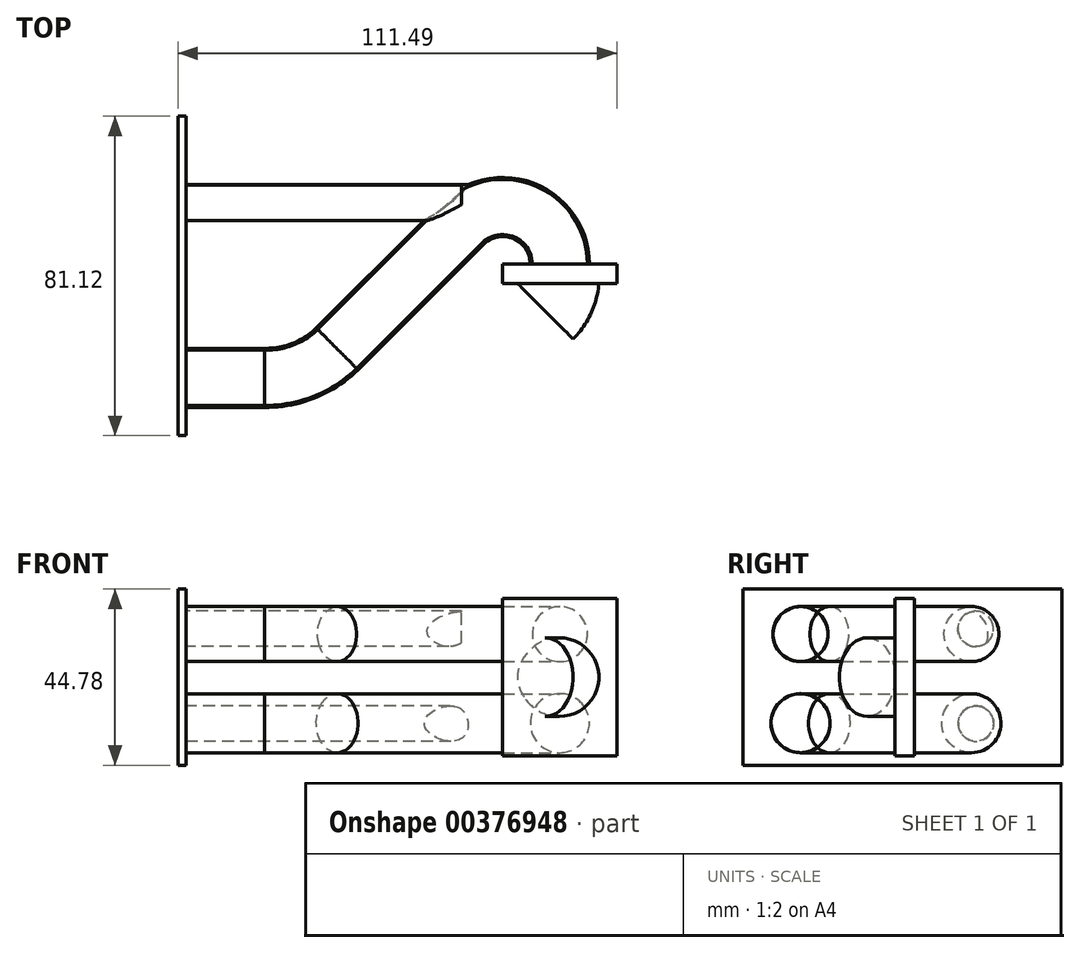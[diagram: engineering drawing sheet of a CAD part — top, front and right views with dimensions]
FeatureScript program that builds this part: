
annotation { "Feature Type Name" : "Feature", "Feature Type Description" : "" }
export const myFeature = defineFeature(function(context is Context, id is Id, definition is map)
    precondition{}
    {
        {
            var Q0;
            Q0=qCreatedBy(makeId("Front.planeOp"),FACE);
            var sketch = newSketch(context, id + "F0", { "sketchPlane" : qUnion([Q0])});
            skCircle(sketch, "E0", {"center": v(0, 0) * mm, "radius": 10 * mm});
            skLineSegment(sketch, "E1", {"start": v(-12.69, 8.58) * mm, "end": v(-12.69, -10.57) * mm});
            skSolve(sketch);
        }
        {
            var Q0;
            Q0=makeQuery(id+"F0.imprint","IMPRINT",FACE,{"disambiguationData":[TD([[makeQuery(id+"F0.imprint","IMPRINT",EDGE,{"derivedFrom":sQuery(id+"F0.wireOp",EDGE,"E0")}),1.0]])]});
            var Q1;
            Q1=sQuery(id+"F0.wireOp",EDGE,"E1");
            revolve(context, id + "F1", {"entities" : qUnion([Q0]), "axis" : qUnion([Q1]), "revolveType" : RevolveType.ONE_DIRECTION, "angle" : 45 * degree});
        }
        {
            var Q0;
            Q0=qCreatedBy(makeId("Front.planeOp"),FACE);
            var sketch = newSketch(context, id + "F2", { "sketchPlane" : qUnion([Q0])});
            skLineSegment(sketch, "E2.bottom", {"start": v(14.5, -20) * mm, "end": v(-14.5, -20) * mm});
            skLineSegment(sketch, "E2.top", {"start": v(14.5, 20) * mm, "end": v(-14.5, 20) * mm});
            skLineSegment(sketch, "E2.left", {"start": v(14.5, -20) * mm, "end": v(14.5, 20) * mm});
            skLineSegment(sketch, "E2.right", {"start": v(-14.5, -20) * mm, "end": v(-14.5, 20) * mm});
            skPoint(sketch, "E2.middle", {"position": v(0, 0) * mm});
            skSolve(sketch);
        }
        {
            var Q0;
            Q0=makeQuery(id+"F2.imprint","IMPRINT",FACE,{"disambiguationData":[TD([[makeQuery(id+"F2.imprint","IMPRINT",EDGE,{"derivedFrom":sQuery(id+"F2.wireOp",EDGE,"E2.bottom")}),-1.0]])]});
            extrude(context, id + "F3", {"entities" : qUnion([Q0]), "operationType" : NewBodyOperationType.ADD, "oppositeDirection" : true, "depth" : 3 * mm, "hasSecondDirection" : true, "secondDirectionOppositeDirection" : false, "secondDirectionDepth" : 1.9 * mm});
        }
        {
            var Q0;
            Q0=makeQuery(id+"F3.opExtrude","CAP_FACE",FACE,{"disambiguationData":[OSD([sQuery(id+"F2.wireOp",EDGE,"E2.bottom"),sQuery(id+"F2.wireOp",EDGE,"E2.top"),sQuery(id+"F2.wireOp",EDGE,"E2.left"),sQuery(id+"F2.wireOp",EDGE,"E2.right")])],"isStart":false});
            var sketch = newSketch(context, id + "F4", { "sketchPlane" : qUnion([Q0])});
            skPoint(sketch, "E3", {"position": v(0, -20) * mm});
            skLineSegment(sketch, "E4", {"start": v(0, -20) * mm, "end": v(0, 0) * mm});
            skPoint(sketch, "E5", {"position": v(0, -10) * mm});
            skPoint(sketch, "E6", {"position": v(0, 0) * mm});
            skSolve(sketch);
        }
        {
            var Q0;
            Q0=makeQuery(id+"F4.imprint","IMPRINT",FACE,{"disambiguationData":[TD([[makeQuery(id+"F4.imprint","IMPRINT",EDGE,{"derivedFrom":makeQuery(id+"F3.opExtrude","CAP_EDGE",EDGE,{"disambiguationData":[OSD([sQuery(id+"F2.wireOp",EDGE,"E2.top")])],"isStart":false})}),-1.0]])]});
            var sketch = newSketch(context, id + "F5", { "sketchPlane" : qUnion([Q0])});
            skCircle(sketch, "E7", {"center": v(0, -11.7) * mm, "radius": 7.5 * mm});
            skSolve(sketch);
        }
        {
            var Q0;
            Q0=makeQuery(id+"F4.imprint","IMPRINT",FACE,{"disambiguationData":[TD([[makeQuery(id+"F4.imprint","IMPRINT",EDGE,{"derivedFrom":makeQuery(id+"F3.opExtrude","CAP_EDGE",EDGE,{"disambiguationData":[OSD([sQuery(id+"F2.wireOp",EDGE,"E2.top")])],"isStart":false})}),-1.0]])]});
            var sketch = newSketch(context, id + "F6", { "sketchPlane" : qUnion([Q0])});
            skCircle(sketch, "E8", {"center": v(0, 10.93) * mm, "radius": 7 * mm});
            skSolve(sketch);
        }
        {
            var Q0;
            Q0 = qSketchRegion(id + "F5", true);
            var Q1;
            Q1=makeQuery(id+"F3.opExtrude","CAP_EDGE",EDGE,{"disambiguationData":[OSD([sQuery(id+"F2.wireOp",EDGE,"E2.right")])],"isStart":false});
            revolve(context, id + "F7", {"operationType" : NewBodyOperationType.ADD, "entities" : qUnion([Q0]), "axis" : qUnion([Q1]), "revolveType" : RevolveType.ONE_DIRECTION, "angle" : 135 * degree});
        }
        {
            var Q0;
            Q0 = qSketchRegion(id + "F6", true);
            var Q1;
            Q1=makeQuery(id+"F3.opExtrude","CAP_EDGE",EDGE,{"disambiguationData":[OSD([sQuery(id+"F2.wireOp",EDGE,"E2.right")])],"isStart":false});
            revolve(context, id + "F8", {"operationType" : NewBodyOperationType.ADD, "entities" : qUnion([Q0]), "axis" : qUnion([Q1]), "revolveType" : RevolveType.ONE_DIRECTION, "angle" : 135 * degree});
        }
        {
            var Q0;
            Q0=makeQuery(id+"F7.opRevolve","CAP_FACE",FACE,{"disambiguationData":[OSD([sQuery(id+"F5.wireOp",EDGE,"E7")])],"isStart":false});
            var Q1;
            Q1=makeQuery(id+"F8.opRevolve","CAP_FACE",FACE,{"disambiguationData":[OSD([sQuery(id+"F6.wireOp",EDGE,"E8")])],"isStart":false});
            extrude(context, id + "F9", {"entities" : qUnion([Q0, Q1]), "operationType" : NewBodyOperationType.ADD, "depth" : 45 * mm});
        }
        {
            var Q0;
            Q0=qCreatedBy(makeId("Front.planeOp"),FACE);
            var sketch = newSketch(context, id + "F10", { "sketchPlane" : qUnion([Q0])});
            skLineSegment(sketch, "E9", {"start": v(-74.63, -11.6) * mm, "end": v(-74.63, 13.78) * mm});
            skSolve(sketch);
        }
        {
            var Q0;
            Q0=makeQuery(id+"F9.opExtrude","CAP_FACE",FACE,{"disambiguationData":[OSD([sQuery(id+"F5.wireOp",EDGE,"E7")])],"isStart":false});
            var Q1;
            Q1=makeQuery(id+"F9.opExtrude","CAP_FACE",FACE,{"disambiguationData":[OSD([sQuery(id+"F6.wireOp",EDGE,"E8")])],"isStart":false});
            var Q2;
            Q2=sQuery(id+"F10.wireOp",EDGE,"E9");
            revolve(context, id + "F11", {"operationType" : NewBodyOperationType.ADD, "entities" : qUnion([Q0, Q1]), "axis" : qUnion([Q2]), "revolveType" : RevolveType.ONE_DIRECTION, "oppositeDirection" : true, "angle" : 45 * degree});
        }
        {
            var Q0;
            Q0=makeQuery(id+"F11.opRevolve","CAP_FACE",FACE,{"disambiguationData":[OSD([sQuery(id+"F5.wireOp",EDGE,"E7")])],"isStart":false});
            var Q1;
            Q1=makeQuery(id+"F11.opRevolve","CAP_FACE",FACE,{"disambiguationData":[OSD([sQuery(id+"F6.wireOp",EDGE,"E8")])],"isStart":false});
            extrude(context, id + "F12", {"entities" : qUnion([Q0, Q1]), "operationType" : NewBodyOperationType.ADD, "depth" : 20 * mm});
        }
        {
            var Q0;
            Q0=makeQuery(id+"F12.opExtrude","CAP_FACE",FACE,{"disambiguationData":[OSD([sQuery(id+"F6.wireOp",EDGE,"E8")])],"isStart":false});
            var sketch = newSketch(context, id + "F13", { "sketchPlane" : qUnion([Q0])});
            skLineSegment(sketch, "E10.bottom", {"start": v(-40.56, -22.4) * mm, "end": v(40.56, -22.4) * mm});
            skLineSegment(sketch, "E10.top", {"start": v(-40.56, 22.4) * mm, "end": v(40.56, 22.4) * mm});
            skLineSegment(sketch, "E10.left", {"start": v(-40.56, -22.4) * mm, "end": v(-40.56, 22.4) * mm});
            skLineSegment(sketch, "E10.right", {"start": v(40.56, -22.4) * mm, "end": v(40.56, 22.4) * mm});
            skPoint(sketch, "E10.middle", {"position": v(0, 0) * mm});
            skSolve(sketch);
        }
        {
            var Q0;
            Q0=makeQuery(id+"F13.imprint","IMPRINT",FACE,{"disambiguationData":[TD([[makeQuery(id+"F13.imprint","IMPRINT",EDGE,{"derivedFrom":makeQuery(id+"F12.opExtrude","CAP_EDGE",EDGE,{"disambiguationData":[OSD([sQuery(id+"F6.wireOp",EDGE,"E8")])],"isStart":false})}),1.0]])]});
            var Q1;
            Q1=makeQuery(id+"F13.imprint","IMPRINT",FACE,{"disambiguationData":[TD([[makeQuery(id+"F13.imprint","IMPRINT",EDGE,{"derivedFrom":sQuery(id+"F13.wireOp",EDGE,"E10.bottom")}),1.0]])]});
            extrude(context, id + "F14", {"entities" : qUnion([Q0, Q1]), "operationType" : NewBodyOperationType.ADD, "depth" : 2 * mm});
        }
        {
            var Q0;
            Q0=makeQuery(id+"F14.opExtrude","CAP_FACE",FACE,{"disambiguationData":[OSD([sQuery(id+"F13.wireOp",EDGE,"E10.bottom"),sQuery(id+"F13.wireOp",EDGE,"E10.top"),sQuery(id+"F13.wireOp",EDGE,"E10.left"),sQuery(id+"F13.wireOp",EDGE,"E10.right")])],"isStart":true});
            var sketch = newSketch(context, id + "F15", { "sketchPlane" : qUnion([Q0])});
            skPoint(sketch, "E11", {"position": v(-25.9, -11.7) * mm});
            skPoint(sketch, "E12", {"position": v(-25.9, 10.93) * mm});
            skLineSegment(sketch, "E13", {"start": v(-25.9, -11.7) * mm, "end": v(40.56, -11.7) * mm});
            skSolve(sketch);
        }
        {
            var Q0;
            {var subQ1=makeQuery(id+"F14.opExtrude","CAP_EDGE",EDGE,{"disambiguationData":[OSD([sQuery(id+"F13.wireOp",EDGE,"E10.bottom")])],"isStart":true});Q0=makeQuery(id+"F15.imprint","IMPRINT",FACE,{"disambiguationData":[TD([[makeQuery(id+"F15.imprint","IMPRINT",EDGE,{"derivedFrom":subQ1}),-1.0]])]});}
            var sketch = newSketch(context, id + "F16", { "sketchPlane" : qUnion([Q0])});
            skCircle(sketch, "E14", {"center": v(18.66, -11.8) * mm, "radius": 4.5 * mm});
            skSolve(sketch);
        }
        {
            var Q0;
            {var subQ1=makeQuery(id+"F14.opExtrude","CAP_EDGE",EDGE,{"disambiguationData":[OSD([sQuery(id+"F13.wireOp",EDGE,"E10.bottom")])],"isStart":true});Q0=makeQuery(id+"F15.imprint","IMPRINT",FACE,{"disambiguationData":[TD([[makeQuery(id+"F15.imprint","IMPRINT",EDGE,{"derivedFrom":subQ1}),-1.0]])]});}
            var sketch = newSketch(context, id + "F17", { "sketchPlane" : qUnion([Q0])});
            skCircle(sketch, "E15", {"center": v(18.59, 12.27) * mm, "radius": 4.5 * mm});
            skSolve(sketch);
        }
        {
            var Q0;
            Q0=makeQuery(id+"F16.imprint","IMPRINT",FACE,{"disambiguationData":[TD([[makeQuery(id+"F16.imprint","IMPRINT",EDGE,{"derivedFrom":sQuery(id+"F16.wireOp",EDGE,"E14")}),1.0]])]});
            extrude(context, id + "F18", {"entities" : qUnion([Q0]), "operationType" : NewBodyOperationType.ADD, "depth" : 85 * mm});
        }
        {
            var Q0;
            Q0=makeQuery(id+"F17.imprint","IMPRINT",FACE,{"disambiguationData":[TD([[makeQuery(id+"F17.imprint","IMPRINT",EDGE,{"derivedFrom":sQuery(id+"F17.wireOp",EDGE,"E15")}),1.0]])]});
            extrude(context, id + "F19", {"entities" : qUnion([Q0]), "operationType" : NewBodyOperationType.ADD, "depth" : 70 * mm});
        }
    });
